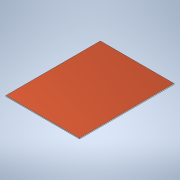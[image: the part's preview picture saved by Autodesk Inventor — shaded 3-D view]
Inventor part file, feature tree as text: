
AUTODESK INVENTOR PART (.ipt)
format: ipt  version: 2020 (Build 240168000, 168)  size: 98,816 bytes
history: native  units: mm
features: other x1, extrude x1, sketch x1
ambient origin geometry x8: Origin, YZ Plane, XZ Plane, XY Plane, X Axis, Y Axis, Z Axis, Center Point
bodies: Body1 (feature_tree)
feature tree (3):
  other  "Sólido1"
  extrude  "Extrusión1"  Depth=1.0mm TaperAngle=0.0deg
  sketch  "Boceto1"  dims[d3=50.0mm d4=1.0mm d5=0.0mm d7=39.0mm]
